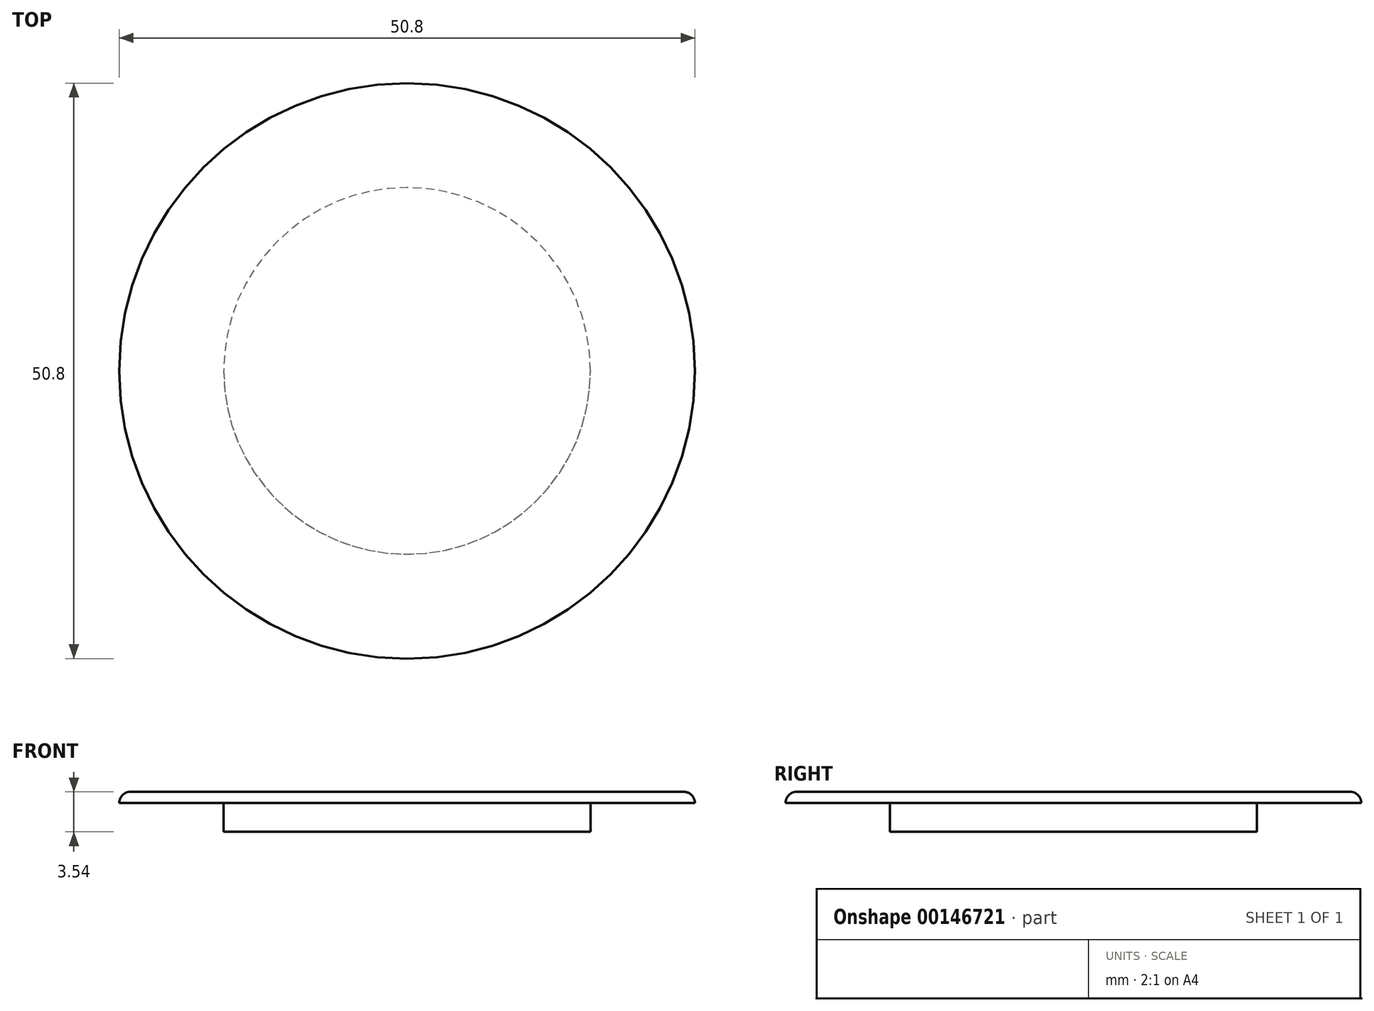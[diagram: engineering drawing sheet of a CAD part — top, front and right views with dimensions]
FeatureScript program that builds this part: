
annotation { "Feature Type Name" : "Feature", "Feature Type Description" : "" }
export const myFeature = defineFeature(function(context is Context, id is Id, definition is map)
    precondition{}
    {
        {
            assignVariable(context, id + "F0", {"name" : "R", "anyValue" : 2});
        }
        {
            var Q0;
            Q0=qCreatedBy(makeId("Top.planeOp"),FACE);
            var sketch = newSketch(context, id + "F1", { "sketchPlane" : qUnion([Q0])});
            skCircle(sketch, "E0", {"center": v(0, 0) * mm, "radius": 25.4 * mm});
            skSolve(sketch);
        }
        {
            var Q0;
            Q0=makeQuery(id+"F1.imprint","IMPRINT",FACE,{"disambiguationData":[TD([[makeQuery(id+"F1.imprint","IMPRINT",EDGE,{"derivedFrom":sQuery(id+"F1.wireOp",EDGE,"E0")}),1.0]])]});
            extrude(context, id + "F2", {"entities" : qUnion([Q0]), "depth" : (getVariable(context, 'R') / 2) * mm});
        }
        {
            var Q0;
            Q0=makeQuery(id+"F2.opExtrude","CAP_EDGE",EDGE,{"disambiguationData":[OSD([sQuery(id+"F1.wireOp",EDGE,"E0")])],"isStart":false});
            fillet(context, id + "F3", {"entities" : qUnion([Q0]), "radius" : (getVariable(context, 'R') / 2) * mm, "tangentPropagation" : true, "allowEdgeOverflow" : false});
        }
        {
            var Q0;
            Q0=makeQuery(id+"F2.opExtrude","CAP_FACE",FACE,{"disambiguationData":[OSD([sQuery(id+"F1.wireOp",EDGE,"E0")])],"isStart":true});
            var sketch = newSketch(context, id + "F4", { "sketchPlane" : qUnion([Q0])});
            skCircle(sketch, "E1", {"center": v(0, 0) * mm, "radius": 16.18 * mm});
            skSolve(sketch);
        }
        {
            var Q0;
            Q0=makeQuery(id+"F4.imprint","IMPRINT",FACE,{"disambiguationData":[TD([[makeQuery(id+"F4.imprint","IMPRINT",EDGE,{"derivedFrom":sQuery(id+"F4.wireOp",EDGE,"E1")}),1.0]])]});
            extrude(context, id + "F5", {"entities" : qUnion([Q0]), "operationType" : NewBodyOperationType.ADD, "depth" : 2.54 * mm});
        }
    });
